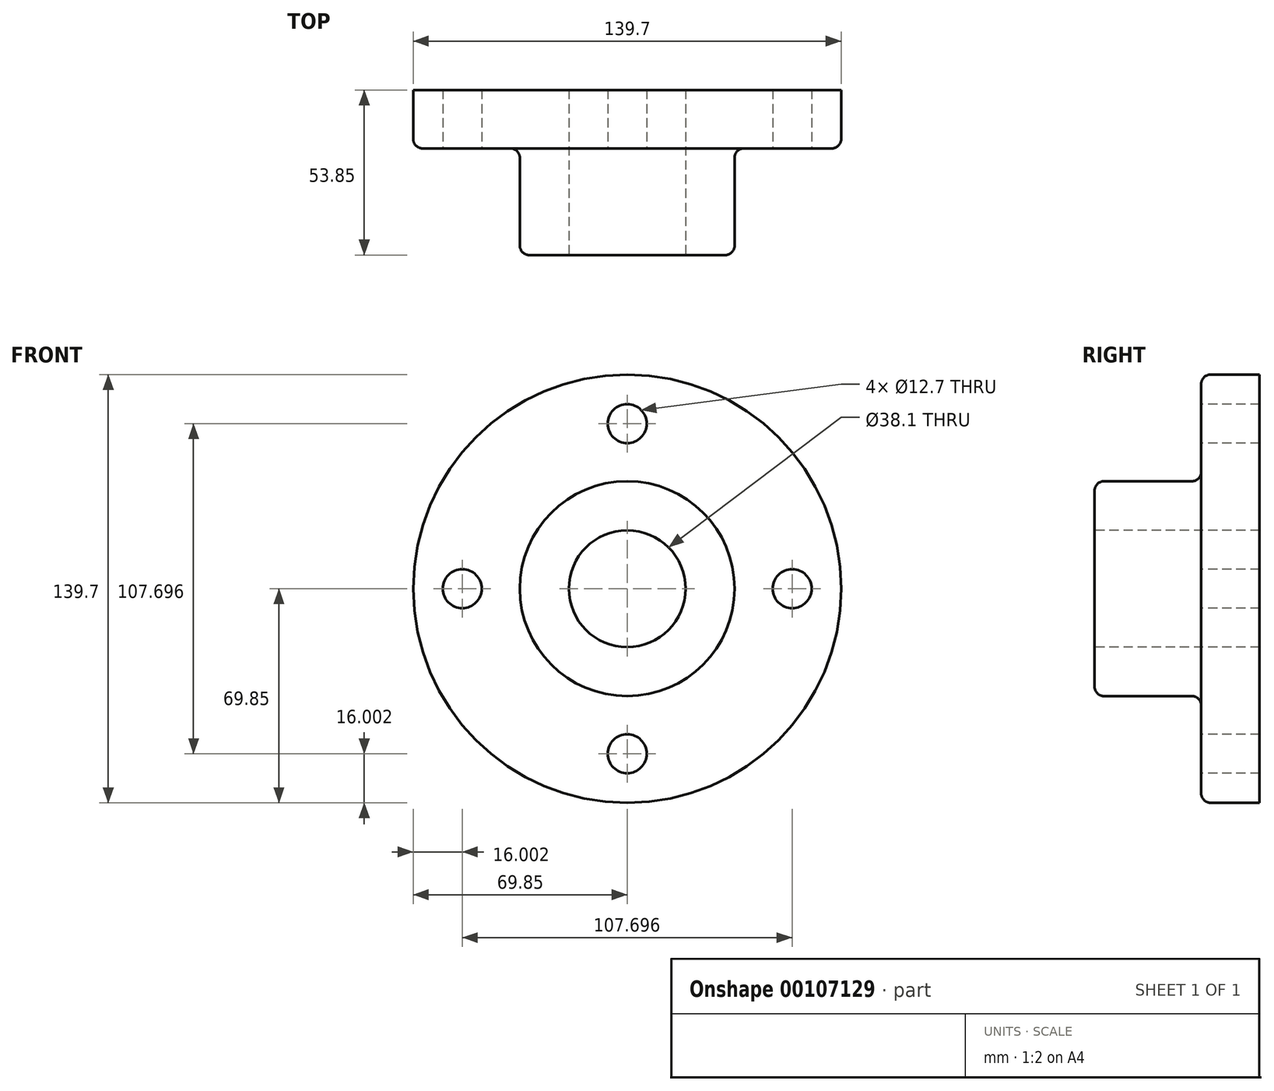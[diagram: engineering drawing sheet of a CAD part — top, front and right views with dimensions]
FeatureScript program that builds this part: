
annotation { "Feature Type Name" : "Feature", "Feature Type Description" : "" }
export const myFeature = defineFeature(function(context is Context, id is Id, definition is map)
    precondition{}
    {
        {
            var Q0;
            Q0=qCreatedBy(makeId("Right.planeOp"),FACE);
            var sketch = newSketch(context, id + "F0", { "sketchPlane" : qUnion([Q0])});
            skLineSegment(sketch, "E0", {"start": v(0, 19.05) * mm, "end": v(53.85, 19.05) * mm});
            skLineSegment(sketch, "E1", {"start": v(53.85, 19.05) * mm, "end": v(53.85, 69.85) * mm});
            skLineSegment(sketch, "E2", {"start": v(53.85, 69.85) * mm, "end": v(34.8, 69.85) * mm});
            skLineSegment(sketch, "E3", {"start": v(34.8, 69.85) * mm, "end": v(34.8, 35.05) * mm});
            skLineSegment(sketch, "E4", {"start": v(34.8, 35.05) * mm, "end": v(0, 35.05) * mm});
            skLineSegment(sketch, "E5", {"start": v(0, 35.05) * mm, "end": v(0, 19.05) * mm});
            skLineSegment(sketch, "E6", {"start": v(0, 0) * mm, "end": v(53.72, 0) * mm, "construction": true});
            skSolve(sketch);
        }
        {
            var Q0;
            Q0=makeQuery(id+"F0.imprint","IMPRINT",FACE,{"disambiguationData":[TD([[makeQuery(id+"F0.imprint","IMPRINT",EDGE,{"derivedFrom":sQuery(id+"F0.wireOp",EDGE,"E0")}),1.0]])]});
            var Q1;
            Q1=sQuery(id+"F0.wireOp",EDGE,"E6");
            revolve(context, id + "F1", {"entities" : qUnion([Q0]), "axis" : qUnion([Q1]), "revolveType" : RevolveType.FULL});
        }
        {
            var Q0;
            Q0=makeQuery(id+"F1.opRevolve","SWEPT_EDGE",EDGE,{"disambiguationData":[OSD([sQuery(id+"F0.wireOp",EDGE,"E4"),sQuery(id+"F0.wireOp",EDGE,"E5")])]});
            var Q1;
            Q1=makeQuery(id+"F1.opRevolve","SWEPT_EDGE",EDGE,{"disambiguationData":[OSD([sQuery(id+"F0.wireOp",EDGE,"E3"),sQuery(id+"F0.wireOp",EDGE,"E4")])]});
            var Q2;
            Q2=makeQuery(id+"F1.opRevolve","SWEPT_EDGE",EDGE,{"disambiguationData":[OSD([sQuery(id+"F0.wireOp",EDGE,"E2"),sQuery(id+"F0.wireOp",EDGE,"E3")])]});
            fillet(context, id + "F2", {"entities" : qUnion([Q0, Q1, Q2]), "radius" : 3.05 * mm, "tangentPropagation" : true, "allowEdgeOverflow" : false});
        }
        {
            var Q0;
            Q0=makeQuery(id+"F1.opRevolve","SWEPT_FACE",FACE,{"disambiguationData":[OSD([sQuery(id+"F0.wireOp",EDGE,"E3")])]});
            var sketch = newSketch(context, id + "F3", { "sketchPlane" : qUnion([Q0])});
            skCircle(sketch, "E7", {"center": v(0, 53.85) * mm, "radius": 6.35 * mm});
            skCircle(sketch, "E8", {"center": v(53.85, 0) * mm, "radius": 6.35 * mm});
            skCircle(sketch, "E9", {"center": v(0, -53.85) * mm, "radius": 6.35 * mm});
            skCircle(sketch, "E10", {"center": v(-53.85, 0) * mm, "radius": 6.35 * mm});
            skSolve(sketch);
        }
        {
            var Q0;
            Q0 = qSketchRegion(id + "F3", true);
            extrude(context, id + "F4", {"entities" : qUnion([Q0]), "operationType" : NewBodyOperationType.REMOVE, "endBound" : BoundingType.THROUGH_ALL, "oppositeDirection" : true, "depth" : 25.4 * mm});
        }
    });
